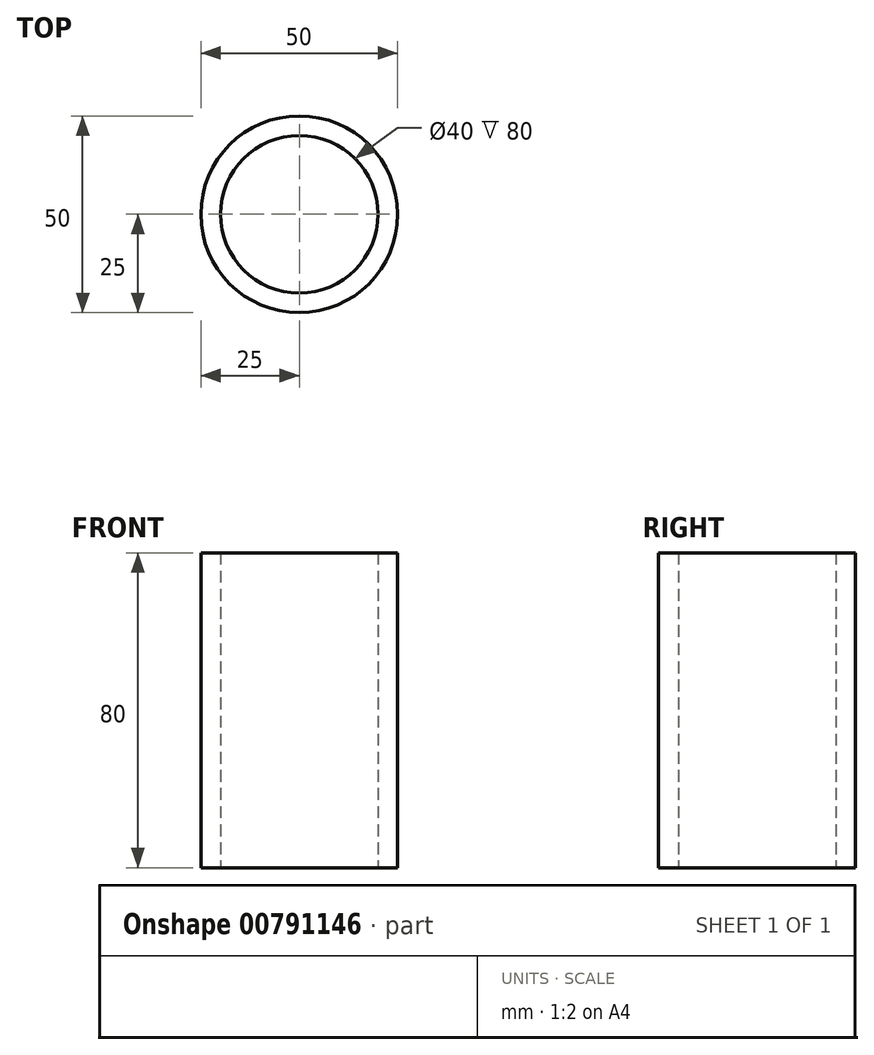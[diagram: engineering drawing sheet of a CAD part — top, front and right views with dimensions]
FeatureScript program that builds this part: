
annotation { "Feature Type Name" : "Feature", "Feature Type Description" : "" }
export const myFeature = defineFeature(function(context is Context, id is Id, definition is map)
    precondition{}
    {
        {
            var Q0;
            Q0=qCreatedBy(makeId("Top.planeOp"),FACE);
            var sketch = newSketch(context, id + "F0", { "sketchPlane" : qUnion([Q0])});
            skCircle(sketch, "E0", {"center": v(0, 0) * mm, "radius": 25 * mm});
            skCircle(sketch, "E1", {"center": v(0, 0) * mm, "radius": 20 * mm});
            skSolve(sketch);
        }
        {
            var Q0;
            Q0=makeQuery(id+"F0.imprint","IMPRINT",FACE,{"disambiguationData":[TD([[makeQuery(id+"F0.imprint","IMPRINT",EDGE,{"derivedFrom":sQuery(id+"F0.wireOp",EDGE,"E0")}),1.0]])]});
            extrude(context, id + "F1", {"entities" : qUnion([Q0]), "depth" : 80 * mm, "offsetDistance" : 25.4 * mm});
        }
    });
